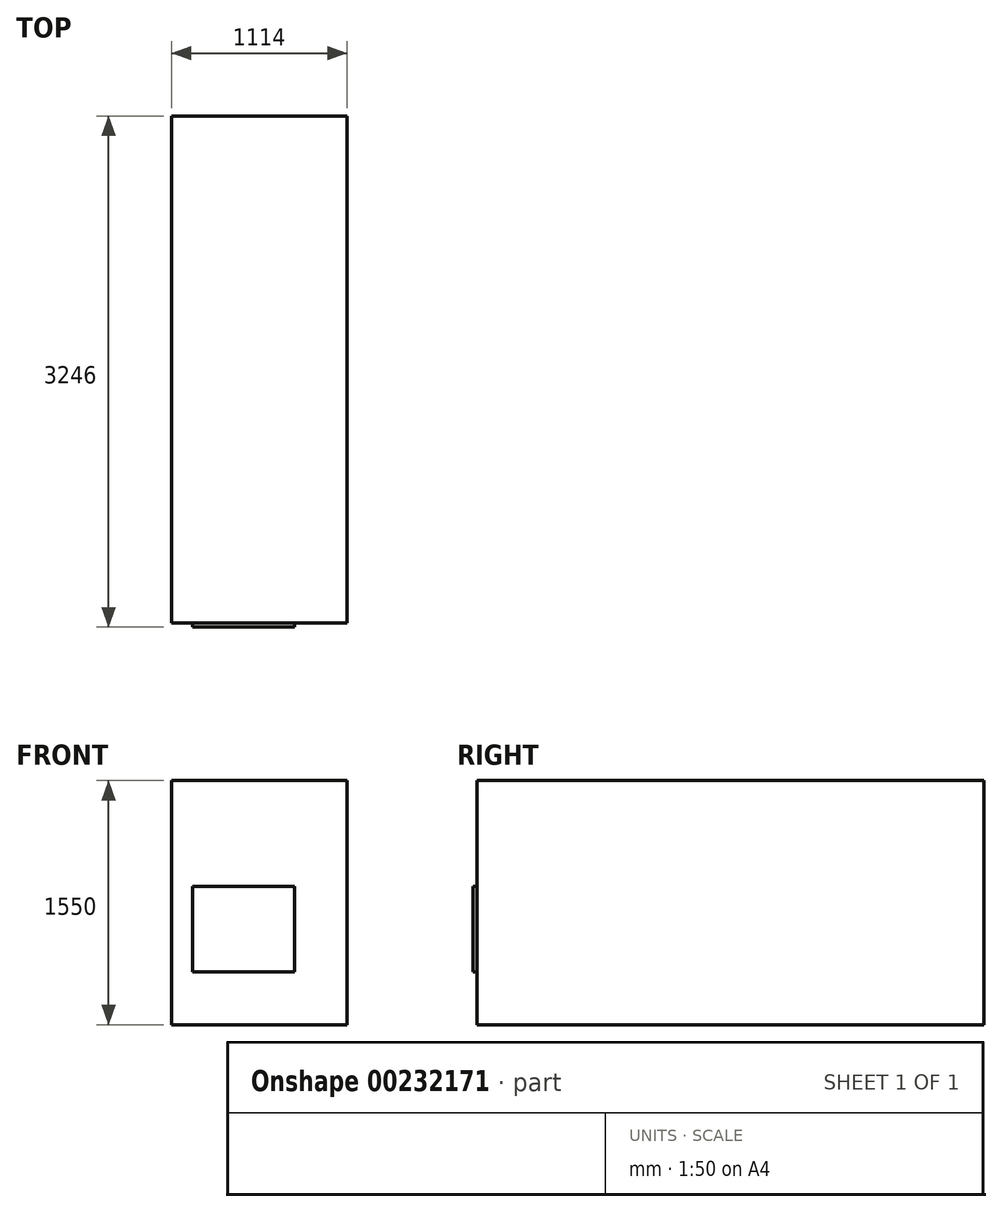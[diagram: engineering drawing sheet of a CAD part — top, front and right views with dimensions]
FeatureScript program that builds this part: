
annotation { "Feature Type Name" : "Feature", "Feature Type Description" : "" }
export const myFeature = defineFeature(function(context is Context, id is Id, definition is map)
    precondition{}
    {
        {
            var Q0;
            Q0=qCreatedBy(makeId("Top.planeOp"),FACE);
            var sketch = newSketch(context, id + "F0", { "sketchPlane" : qUnion([Q0])});
            skLineSegment(sketch, "E0.bottom", {"start": v(0, 0) * mm, "end": v(1114, 0) * mm});
            skLineSegment(sketch, "E0.top", {"start": v(0, 3221) * mm, "end": v(1114, 3221) * mm});
            skLineSegment(sketch, "E0.left", {"start": v(0, 0) * mm, "end": v(0, 3221) * mm});
            skLineSegment(sketch, "E0.right", {"start": v(1114, 0) * mm, "end": v(1114, 3221) * mm});
            skSolve(sketch);
        }
        {
            var Q0;
            Q0 = qSketchRegion(id + "F0", true);
            extrude(context, id + "F1", {"entities" : qUnion([Q0]), "depth" : 1550 * mm});
        }
        {
            var Q0;
            Q0=makeQuery(id+"F1.opExtrude","SWEPT_FACE",FACE,{"disambiguationData":[OSD([sQuery(id+"F0.wireOp",EDGE,"E0.bottom")])]});
            var sketch = newSketch(context, id + "F2", { "sketchPlane" : qUnion([Q0])});
            skLineSegment(sketch, "E1.bottom", {"start": v(131.95, 878.24) * mm, "end": v(780.96, 878.24) * mm});
            skLineSegment(sketch, "E1.top", {"start": v(131.95, 336.23) * mm, "end": v(780.96, 336.23) * mm});
            skLineSegment(sketch, "E1.left", {"start": v(131.95, 878.24) * mm, "end": v(131.95, 336.23) * mm});
            skLineSegment(sketch, "E1.right", {"start": v(780.96, 878.24) * mm, "end": v(780.96, 336.23) * mm});
            skSolve(sketch);
        }
        {
            var Q0;
            Q0 = qSketchRegion(id + "F2", true);
            extrude(context, id + "F3", {"entities" : qUnion([Q0]), "operationType" : NewBodyOperationType.ADD, "depth" : 25 * mm});
        }
    });
